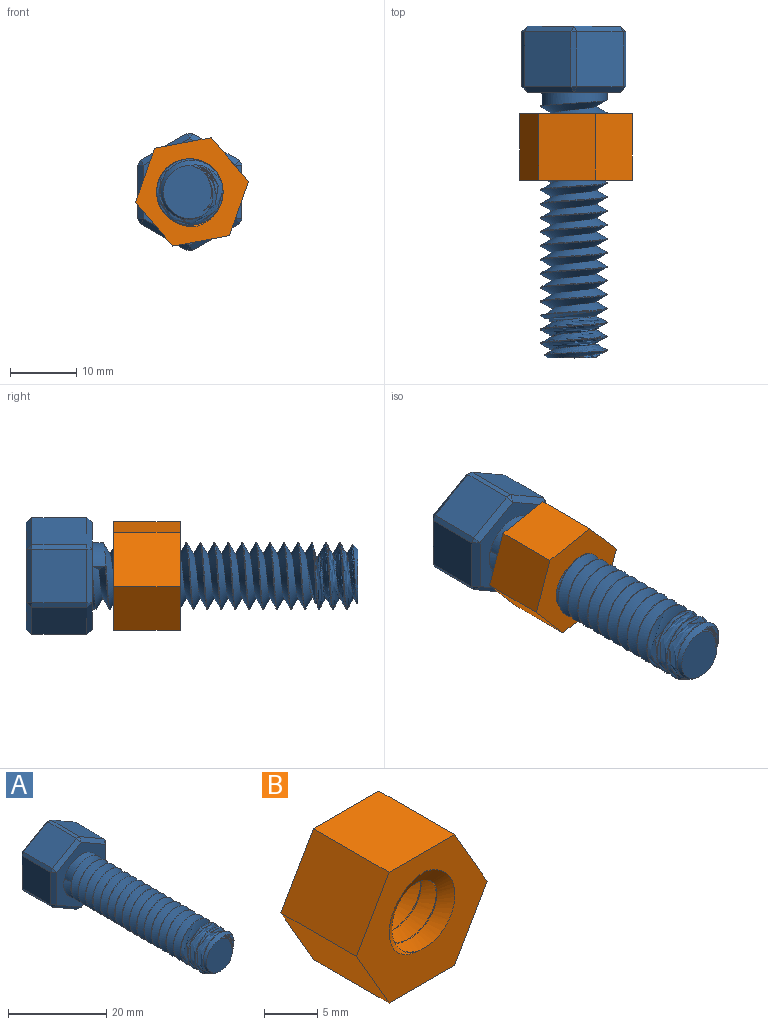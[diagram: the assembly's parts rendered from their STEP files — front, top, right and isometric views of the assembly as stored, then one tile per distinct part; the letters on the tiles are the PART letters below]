
ASSEMBLY  parts=2 mates=1
PART A: 45 faces, bbox 16x51.5x17.9 mm
  f0: cylinder r=5mm len=39mm, axis (0,1,0), area 95.4mm2, adj f8,f10,f12,f13,f14
  f1: plane 8.29x7.78mm, normal (0,-1,0), area 46.8mm2, adj f12,f13,f14
  f2: plane 8.27x6.98mm, normal (-0.5,0,-0.87), area 66.7mm2, adj f15,f19,f20,f21
  f3: plane 8.27x6.98mm, normal (0.5,0,-0.87), area 66.7mm2, adj f18,f19,f28,f29
  f4: plane 8.27x8.06mm, normal (1,0,0), area 66.7mm2, adj f27,f28,f38,f39
  f5: plane 8.27x6.98mm, normal (0.5,0,0.87), area 66.7mm2, adj f33,f38,f41,f44
  f6: plane 8.27x6.98mm, normal (-0.5,0,0.87), area 66.7mm2, adj f31,f32,f40,f41
  f7: plane 8.27x8.06mm, normal (-1,0,0), area 66.7mm2, adj f21,f22,f30,f31
  f8: plane 16.13x13.96mm, normal (0,-1,0), area 90.3mm2, adj f0,f11,f20,f29,f30,f39,f40,f44
  f9: plane 16.13x13.96mm, normal (0,1,0), area 168.9mm2, adj f15,f18,f22,f27,f32,f33
  f10: plane 2x1.66mm, normal (-0.29,0,-0.96), area 1.7mm2, adj f0,f11,f12,f13
  f11: cylinder r=5mm len=0.7mm, axis (0,1,0), area 0mm2, adj f8,f10,f13
  f12: bspline ~40.55x11.55mm, area 943.7mm2, adj f0,f1,f10,f13,f14
  f13: bspline ~40.9x11.55mm, area 970.9mm2, adj f0,f1,f10,f11,f12,f14
  f14: cone r=4mm half-angle=45deg, axis (0,1,0), area 12.5mm2, adj f0,f1,f12,f13
  f15: plane 7.42x4.78mm, normal (-0.35,0.71,-0.61), area 9.9mm2, adj f2,f9,f16,f17
  f16: plane 0.87x0.87mm, normal (0,0.65,-0.76), area 0.5mm2, adj f15,f18,f19
  f17: plane 0.87x0.87mm, normal (-0.65,0.65,-0.38), area 0.5mm2, adj f15,f21,f22
  f18: plane 7.42x4.78mm, normal (0.35,0.71,-0.61), area 9.9mm2, adj f3,f9,f16,f23
  f19: plane 8.27x0.87mm, normal (0,0,-1), area 7.2mm2, adj f2,f3,f16,f24
  f20: plane 7.42x4.78mm, normal (-0.35,-0.71,-0.61), area 9.9mm2, adj f2,f8,f24,f25
  f21: plane 8.27x0.75mm, normal (-0.87,0,-0.5), area 7.2mm2, adj f2,f7,f17,f25
  f22: plane 8.06x0.87mm, normal (-0.71,0.71,0), area 9.9mm2, adj f7,f9,f17,f26
  f23: plane 0.87x0.87mm, normal (0.65,0.65,-0.38), area 0.5mm2, adj f18,f27,f28
  f24: plane 0.87x0.87mm, normal (0,-0.65,-0.76), area 0.5mm2, adj f19,f20,f29
  f25: plane 0.87x0.87mm, normal (-0.65,-0.65,-0.38), area 0.5mm2, adj f20,f21,f30
  f26: plane 0.87x0.87mm, normal (-0.65,0.65,0.38), area 0.5mm2, adj f22,f31,f32
  f27: plane 8.06x0.87mm, normal (0.71,0.71,0), area 9.9mm2, adj f4,f9,f23,f34
  f28: plane 8.27x0.75mm, normal (0.87,0,-0.5), area 7.2mm2, adj f3,f4,f23,f35
  f29: plane 7.42x4.78mm, normal (0.35,-0.71,-0.61), area 9.9mm2, adj f3,f8,f24,f35
  f30: plane 8.06x0.87mm, normal (-0.71,-0.71,0), area 9.9mm2, adj f7,f8,f25,f36
  f31: plane 8.27x0.75mm, normal (-0.87,0,0.5), area 7.2mm2, adj f6,f7,f26,f36
  f32: plane 7.42x4.78mm, normal (-0.35,0.71,0.61), area 9.9mm2, adj f6,f9,f26,f37
  f33: plane 7.42x4.78mm, normal (0.35,0.71,0.61), area 9.9mm2, adj f5,f9,f34,f37
  f34: plane 0.87x0.87mm, normal (0.65,0.65,0.38), area 0.5mm2, adj f27,f33,f38
  f35: plane 0.87x0.87mm, normal (0.65,-0.65,-0.38), area 0.5mm2, adj f28,f29,f39
  f36: plane 0.87x0.87mm, normal (-0.65,-0.65,0.38), area 0.5mm2, adj f30,f31,f40
  f37: plane 0.87x0.87mm, normal (0,0.65,0.76), area 0.5mm2, adj f32,f33,f41
  f38: plane 8.27x0.75mm, normal (0.87,0,0.5), area 7.2mm2, adj f4,f5,f34,f42
  f39: plane 8.06x0.87mm, normal (0.71,-0.71,0), area 9.9mm2, adj f4,f8,f35,f42
  f40: plane 7.42x4.78mm, normal (-0.35,-0.71,0.61), area 9.9mm2, adj f6,f8,f36,f43
  f41: plane 8.27x0.87mm, normal (0,0,1), area 7.2mm2, adj f5,f6,f37,f43
  f42: plane 0.87x0.87mm, normal (0.65,-0.65,0.38), area 0.5mm2, adj f38,f39,f44
  f43: plane 0.87x0.87mm, normal (0,-0.65,0.76), area 0.5mm2, adj f40,f41,f44
  f44: plane 7.42x4.78mm, normal (0.35,-0.71,0.61), area 9.9mm2, adj f5,f8,f42,f43
PART B: 11 faces, bbox 18.7x13.9x16.4 mm
  f0: plane 10x7.5mm, normal (-0.87,0,0.5), area 86.6mm2, adj f1,f6,f7,f8
  f1: plane 10x7.5mm, normal (-0.87,0,-0.5), area 86.6mm2, adj f0,f2,f7,f8
  f2: plane 10x8.66mm, normal (0,0,-1), area 86.6mm2, adj f1,f3,f7,f8
  f3: plane 10x7.5mm, normal (0.87,0,-0.5), area 86.6mm2, adj f2,f4,f7,f8
  f4: plane 10x7.5mm, normal (0.87,0,0.5), area 86.6mm2, adj f3,f6,f7,f8
  f5: cylinder r=3.5mm len=10mm, axis (0,1,0), area 10.8mm2, adj f7,f8,f9,f10
  f6: plane 10x8.66mm, normal (0,0,1), area 86.6mm2, adj f0,f4,f7,f8
  f7: plane 18.69x16.37mm, normal (0,-1,0), area 135.2mm2, adj f0,f1,f2,f3,f4,f5,f6,f9
  f8: plane 18.65x16.33mm, normal (0,1,0), area 135.2mm2, adj f0,f1,f2,f3,f4,f5,f6,f9
  f9: bspline ~12.2x12.08mm, area 262mm2, adj f5,f7,f8,f10
  f10: bspline ~12.55x12.08mm, area 261.9mm2, adj f5,f7,f8,f9
PLACE A t=(-13.87,17.41,-0.31)mm fixed
PLACE B rot(axis=(0,1,0),169.4deg) t=(-13.55,4.2,-0.3)mm
MATE cylindrical B.f8 <-> A.f0  axis (0,1,0) through (-13.87,4.2,-0.31)mm
